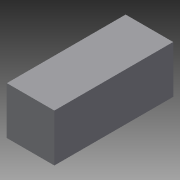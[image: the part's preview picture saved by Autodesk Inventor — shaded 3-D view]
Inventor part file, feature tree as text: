
AUTODESK INVENTOR PART (.ipt)
format: ipt  version: 2015 (Build 190159000, 159)  size: 68,608 bytes
history: native  units: mm
features: other x1, extrude x1, sketch x1
ambient origin geometry x8: Origin, YZ Plane, XZ Plane, XY Plane, X Axis, Y Axis, Z Axis, Center Point
bodies: Body1 (feature_tree)
feature tree (3):
  other  "ソリッド1"
  extrude  "押し出し1"  Depth=30.0mm
  sketch  "スケッチ1"
